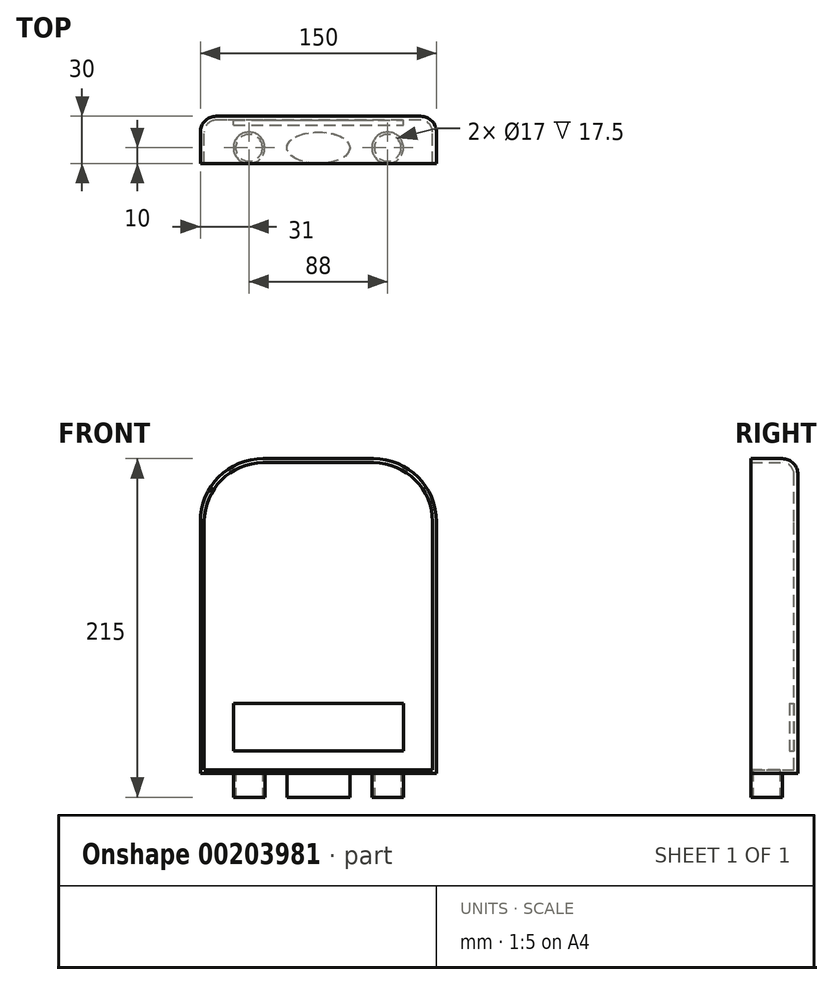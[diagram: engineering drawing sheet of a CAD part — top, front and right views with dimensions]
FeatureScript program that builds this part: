
annotation { "Feature Type Name" : "Feature", "Feature Type Description" : "" }
export const myFeature = defineFeature(function(context is Context, id is Id, definition is map)
    precondition{}
    {
        {
            var Q0;
            Q0=qCreatedBy(makeId("Front.planeOp"),FACE);
            var sketch = newSketch(context, id + "F0", { "sketchPlane" : qUnion([Q0])});
            skLineSegment(sketch, "E0.bottom", {"start": v(75, -100) * mm, "end": v(-75, -100) * mm});
            skLineSegment(sketch, "E0.top", {"start": v(35, 100) * mm, "end": v(-35, 100) * mm});
            skLineSegment(sketch, "E0.left", {"start": v(75, -100) * mm, "end": v(75, 60) * mm});
            skLineSegment(sketch, "E0.right", {"start": v(-75, -100) * mm, "end": v(-75, 60) * mm});
            skPoint(sketch, "E0.middle", {"position": v(0, 0) * mm});
            skPoint(sketch, "E1.visualSharp", {"position": v(-75, 100) * mm});
            skArc(sketch, "E1.filletArc", {"start": v(-35, 100) * mm, "mid": v(-63.28, 88.28) * mm, "end": v(-75, 60) * mm});
            skPoint(sketch, "E2.visualSharp", {"position": v(75, 100) * mm});
            skArc(sketch, "E2.filletArc", {"start": v(75, 60) * mm, "mid": v(63.28, 88.28) * mm, "end": v(35, 100) * mm});
            skSolve(sketch);
        }
        {
            var Q0;
            Q0 = qSketchRegion(id + "F0", true);
            extrude(context, id + "F1", {"entities" : qUnion([Q0]), "depth" : 30 * mm});
        }
        {
            var Q0;
            Q0=makeQuery(id+"F1.opExtrude","CAP_EDGE",EDGE,{"disambiguationData":[OSD([sQuery(id+"F0.wireOp",EDGE,"E0.right")])],"isStart":true});
            var Q1;
            Q1=makeQuery(id+"F1.opExtrude","CAP_EDGE",EDGE,{"disambiguationData":[OSD([sQuery(id+"F0.wireOp",EDGE,"E0.left")])],"isStart":true});
            var Q2;
            Q2=makeQuery(id+"F1.opExtrude","CAP_EDGE",EDGE,{"disambiguationData":[OSD([sQuery(id+"F0.wireOp",EDGE,"E2.filletArc")])],"isStart":true});
            var Q3;
            Q3=makeQuery(id+"F1.opExtrude","CAP_EDGE",EDGE,{"disambiguationData":[OSD([sQuery(id+"F0.wireOp",EDGE,"E0.top")])],"isStart":true});
            var Q4;
            Q4=makeQuery(id+"F1.opExtrude","CAP_EDGE",EDGE,{"disambiguationData":[OSD([sQuery(id+"F0.wireOp",EDGE,"E1.filletArc")])],"isStart":true});
            fillet(context, id + "F2", {"entities" : qUnion([Q0, Q1, Q2, Q3, Q4]), "radius" : 10 * mm, "tangentPropagation" : true, "allowEdgeOverflow" : false});
        }
        {
            var Q0;
            Q0=makeQuery(id+"F1.opExtrude","CAP_FACE",FACE,{"disambiguationData":[OSD([sQuery(id+"F0.wireOp",EDGE,"E0.bottom"),sQuery(id+"F0.wireOp",EDGE,"E0.top"),sQuery(id+"F0.wireOp",EDGE,"E0.left"),sQuery(id+"F0.wireOp",EDGE,"E0.right")])],"isStart":false});
            shell(context, id + "F3", {"entities" : qUnion([Q0]), "thickness" : 2.5 * mm});
        }
        {
            var Q0;
            Q0=makeQuery(id+"F1.opExtrude","SWEPT_FACE",FACE,{"disambiguationData":[OSD([sQuery(id+"F0.wireOp",EDGE,"E0.bottom")])]});
            var sketch = newSketch(context, id + "F4", { "sketchPlane" : qUnion([Q0])});
            skEllipse(sketch, "E3", {"center": v(0, 20) * mm, "majorRadius": 20 * mm, "minorRadius": 10 * mm, "majorAxis": v(1, 0)});
            skPoint(sketch, "E3.centerSnap0", {"position": v(-75, 20) * mm});
            skPoint(sketch, "E3.centerSnap1", {"position": v(0, 30) * mm});
            skCircle(sketch, "E4", {"center": v(-44, 20) * mm, "radius": 10 * mm});
            skCircle(sketch, "E5.MirrorC", {"center": v(44, 20) * mm, "radius": 10 * mm});
            skSolve(sketch);
        }
        {
            var Q0;
            Q0 = qSketchRegion(id + "F4", true);
            extrude(context, id + "F5", {"entities" : qUnion([Q0]), "operationType" : NewBodyOperationType.ADD, "depth" : 15 * mm});
        }
        {
            var Q0;
            Q0=makeQuery(id+"F5.opExtrude","CAP_FACE",FACE,{"disambiguationData":[OSD([sQuery(id+"F4.wireOp",EDGE,"E4")])],"isStart":false});
            var sketch = newSketch(context, id + "F6", { "sketchPlane" : qUnion([Q0])});
            skCircle(sketch, "E6", {"center": v(-44, 20) * mm, "radius": 8.5 * mm});
            skFitSpline(sketch, "E7.0", {"points": [v(18.32, 13.62) * mm, v(18.59, 15) * mm, v(18.32, 16.38) * mm, v(17.6, 17.62) * mm, v(16.65, 18.62) * mm, v(15.46, 19.6) * mm, v(13.57, 20.77) * mm, v(11.2, 21.74) * mm, v(9.05, 22.38) * mm, v(6.8, 22.92) * mm, v(4.39, 23.28) * mm, v(1.9, 23.47) * mm, v(0, 23.52) * mm, v(-1.9, 23.47) * mm, v(-4.39, 23.28) * mm, v(-6.8, 22.92) * mm, v(-9.05, 22.38) * mm, v(-11.2, 21.74) * mm, v(-13.57, 20.77) * mm, v(-15.46, 19.6) * mm, v(-16.65, 18.62) * mm, v(-17.6, 17.62) * mm, v(-18.32, 16.38) * mm, v(-18.59, 15) * mm, v(-18.32, 13.62) * mm, v(-17.6, 12.38) * mm, v(-16.65, 11.38) * mm, v(-15.46, 10.4) * mm, v(-13.57, 9.23) * mm, v(-11.2, 8.26) * mm, v(-9.05, 7.62) * mm, v(-6.8, 7.08) * mm, v(-4.39, 6.72) * mm, v(-1.9, 6.53) * mm, v(0, 6.48) * mm, v(1.9, 6.53) * mm, v(4.39, 6.72) * mm, v(6.8, 7.08) * mm, v(9.05, 7.62) * mm, v(11.2, 8.26) * mm, v(13.57, 9.23) * mm, v(15.46, 10.4) * mm, v(16.65, 11.38) * mm, v(17.6, 12.38) * mm, v(18.32, 13.62) * mm, v(18.59, 15) * mm, v(18.32, 16.38) * mm, v(18.32, 13.62) * mm]});
            skCircle(sketch, "E8.MirrorC", {"center": v(44, 20) * mm, "radius": 8.5 * mm});
            skSolve(sketch);
        }
        {
            var Q0;
            Q0 = qSketchRegion(id + "F6", true);
            var Q1;
            {var subQ0=sQuery(id+"F0.wireOp",EDGE,"E0.bottom");Q1=makeQuery(id+"F3.opShell","OFFSET_FACE",FACE,{"disambiguationData":[OSD([subQ0]),TDD([makeQuery(id+"F1.opExtrude","SWEPT_FACE",FACE,{"disambiguationData":[OSD([subQ0])]})])]});}
            extrude(context, id + "F7", {"entities" : qUnion([Q0]), "operationType" : NewBodyOperationType.REMOVE, "endBound" : BoundingType.UP_TO_SURFACE, "oppositeDirection" : true, "endBoundEntityFace" : qUnion([Q1]), "depth" : 25 * mm});
        }
        {
            var Q0;
            Q0=makeQuery(id+"F3.opShell","OFFSET_FACE",FACE,{"disambiguationData":[OSD([sQuery(id+"F0.wireOp",EDGE,"E0.bottom"),sQuery(id+"F0.wireOp",EDGE,"E0.top"),sQuery(id+"F0.wireOp",EDGE,"E0.left"),sQuery(id+"F0.wireOp",EDGE,"E0.right"),sQuery(id+"F0.wireOp",EDGE,"E1.filletArc"),sQuery(id+"F0.wireOp",EDGE,"E2.filletArc")])]});
            var sketch = newSketch(context, id + "F8", { "sketchPlane" : qUnion([Q0])});
            skLineSegment(sketch, "E9.bottom", {"start": v(-54, -55.5) * mm, "end": v(54, -55.5) * mm});
            skLineSegment(sketch, "E9.top", {"start": v(-54, -85.5) * mm, "end": v(54, -85.5) * mm});
            skLineSegment(sketch, "E9.left", {"start": v(-54, -55.5) * mm, "end": v(-54, -85.5) * mm});
            skLineSegment(sketch, "E9.right", {"start": v(54, -55.5) * mm, "end": v(54, -85.5) * mm});
            skSolve(sketch);
        }
        {
            var Q0;
            Q0 = qSketchRegion(id + "F8", true);
            extrude(context, id + "F9", {"entities" : qUnion([Q0]), "depth" : 3 * mm});
        }
    });
